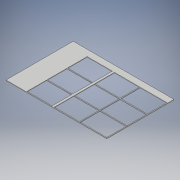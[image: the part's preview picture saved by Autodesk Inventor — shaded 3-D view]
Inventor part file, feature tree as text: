
AUTODESK INVENTOR PART (.ipt)
format: ipt  version: 2019.4 (Build 234330000, 330)  size: 146,432 bytes
history: native  units: mm
features: extrude x1, sketch x1
ambient origin geometry x8: Origin, YZ Plane, XZ Plane, XY Plane, X Axis, Y Axis, Z Axis, Center Point
bodies: Solid1 (feature_tree)
feature tree (2):
  extrude  "Extrusion1"  Depth=1219.2mm
  sketch  "Sketch1"  dims[d0=1828.8mm d1=1219.2mm d2=12.7mm d3=12.7mm d4=482.6mm d5=355.6mm d6=30.0mm d8=368.3mm d9=10.0mm d11=10.0mm d13=12.7mm d14=457.2mm d15=355.6mm d16=30.0mm d18=368.3mm d19=20.0mm d21=495.3mm d24=10.0mm d25=0.0mm]
